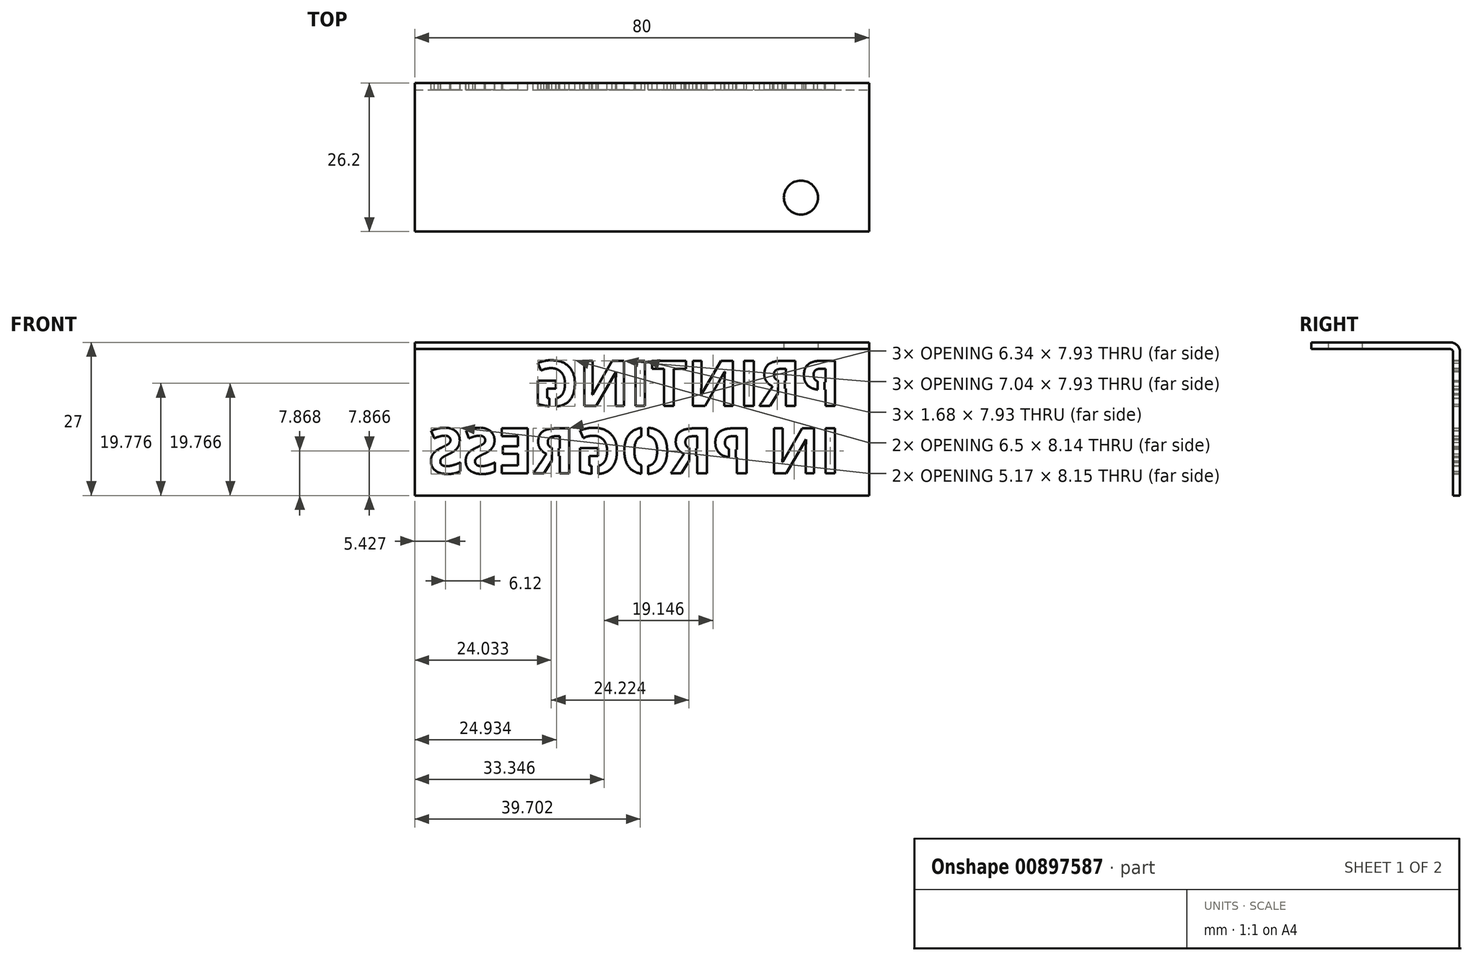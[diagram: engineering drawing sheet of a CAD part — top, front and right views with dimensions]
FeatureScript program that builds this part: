
annotation { "Feature Type Name" : "Feature", "Feature Type Description" : "" }
export const myFeature = defineFeature(function(context is Context, id is Id, definition is map)
    precondition{}
    {
        {
            var Q0;
            Q0=qCreatedBy(makeId("Right.planeOp"),FACE);
            var sketch = newSketch(context, id + "F0", { "sketchPlane" : qUnion([Q0])});
            skLineSegment(sketch, "E0", {"start": v(0, 0) * mm, "end": v(0, 25.8) * mm});
            skLineSegment(sketch, "E1", {"start": v(0, 25.8) * mm, "end": v(-25, 25.8) * mm});
            skLineSegment(sketch, "E2", {"start": v(-25, 25.8) * mm, "end": v(-25, 27) * mm});
            skLineSegment(sketch, "E3", {"start": v(-25, 27) * mm, "end": v(1.2, 27) * mm});
            skLineSegment(sketch, "E4", {"start": v(1.2, 27) * mm, "end": v(1.2, 0) * mm});
            skLineSegment(sketch, "E5", {"start": v(1.2, 0) * mm, "end": v(0, 0) * mm});
            skSolve(sketch);
        }
        {
            var Q0;
            Q0 = qSketchRegion(id + "F0", true);
            extrude(context, id + "F1", {"entities" : qUnion([Q0]), "oppositeDirection" : true, "depth" : 80 * mm, "offsetDistance" : 25 * mm});
        }
        {
            var Q0;
            Q0=makeQuery(id+"F1.opExtrude","SWEPT_EDGE",EDGE,{"disambiguationData":[OSD([sQuery(id+"F0.wireOp",EDGE,"E0"),sQuery(id+"F0.wireOp",EDGE,"E1")])]});
            fillet(context, id + "F2", {"entities" : qUnion([Q0]), "radius" : 0.5 * mm, "tangentPropagation" : true, "allowEdgeOverflow" : false});
        }
        {
            var Q0;
            Q0=makeQuery(id+"F1.opExtrude","SWEPT_EDGE",EDGE,{"disambiguationData":[OSD([sQuery(id+"F0.wireOp",EDGE,"E3"),sQuery(id+"F0.wireOp",EDGE,"E4")])]});
            fillet(context, id + "F3", {"entities" : qUnion([Q0]), "radius" : 1.7 * mm, "tangentPropagation" : true, "allowEdgeOverflow" : false});
        }
        {
            var Q0;
            Q0=makeQuery(id+"F1.opExtrude","SWEPT_FACE",FACE,{"disambiguationData":[OSD([sQuery(id+"F0.wireOp",EDGE,"E1")])]});
            var sketch = newSketch(context, id + "F4", { "sketchPlane" : qUnion([Q0])});
            skCircle(sketch, "E6", {"center": v(-12, 19) * mm, "radius": 3 * mm});
            skSolve(sketch);
        }
        {
            var Q0;
            Q0 = qSketchRegion(id + "F4", true);
            extrude(context, id + "F5", {"entities" : qUnion([Q0]), "operationType" : NewBodyOperationType.REMOVE, "endBound" : BoundingType.THROUGH_ALL, "oppositeDirection" : true, "depth" : 25 * mm, "offsetDistance" : 25 * mm});
        }
        {
            var Q0;
            Q0=makeQuery(id+"F1.opExtrude","SWEPT_FACE",FACE,{"disambiguationData":[OSD([sQuery(id+"F0.wireOp",EDGE,"E4")])]});
            var sketch = newSketch(context, id + "F6", { "sketchPlane" : qUnion([Q0])});
            skText(sketch, "E7", { "text": "PRINTING\n", "fontName": "OpenSans-Bold.ttf"});
            skText(sketch, "E8", { "text": "IN PROGRESS", "fontName": "OpenSans-Bold.ttf"});
            const initialGuessF6  = {"E7": [0.005, 0.0158, 1, 0, 0.008], "E8": [0.005, 0.0039, 1, 0, 0.008]};
            skSetInitialGuess(sketch, initialGuessF6);
            skSolve(sketch);
        }
        {
            var Q0;
            Q0 = qSketchRegion(id + "F6", true);
            extrude(context, id + "F7", {"entities" : qUnion([Q0]), "operationType" : NewBodyOperationType.REMOVE, "oppositeDirection" : true, "depth" : 25 * mm, "offsetDistance" : 25 * mm});
        }
        {
            var Q0;
            {var subQ0=sQuery(id+"F0.wireOp",EDGE,"E5");var subQ1=sQuery(id+"F0.wireOp",EDGE,"E4");Q0=makeQuery(id+"F7.boolean.opBoolean","SPLIT",FACE,{"disambiguationData":[TD([makeQuery(id+"F1.opExtrude","SWEPT_FACE",FACE,{"disambiguationData":[OSD([subQ0])]})])],"derivedFrom":makeQuery(id+"F1.opExtrude","SWEPT_FACE",FACE,{"disambiguationData":[OSD([subQ1])]})});}
            var sketch = newSketch(context, id + "F8", { "sketchPlane" : qUnion([Q0])});
            skLineSegment(sketch, "E9.bottom", {"start": v(7.88, 21.02) * mm, "end": v(9.08, 21.02) * mm});
            skLineSegment(sketch, "E9.top", {"start": v(7.88, 16.73) * mm, "end": v(9.08, 16.73) * mm});
            skLineSegment(sketch, "E9.left", {"start": v(7.88, 21.02) * mm, "end": v(7.88, 16.73) * mm});
            skLineSegment(sketch, "E9.right", {"start": v(9.08, 21.02) * mm, "end": v(9.08, 16.73) * mm});
            skLineSegment(sketch, "E10.bottom", {"start": v(14.86, 21.26) * mm, "end": v(16.06, 21.26) * mm});
            skLineSegment(sketch, "E10.top", {"start": v(14.86, 17.16) * mm, "end": v(16.06, 17.16) * mm});
            skLineSegment(sketch, "E10.left", {"start": v(14.86, 21.26) * mm, "end": v(14.86, 17.16) * mm});
            skLineSegment(sketch, "E10.right", {"start": v(16.06, 21.26) * mm, "end": v(16.06, 17.16) * mm});
            skLineSegment(sketch, "E11.bottom", {"start": v(55.08, 17.67) * mm, "end": v(56.28, 17.67) * mm});
            skLineSegment(sketch, "E11.top", {"start": v(55.08, 14.77) * mm, "end": v(56.28, 14.77) * mm});
            skLineSegment(sketch, "E11.left", {"start": v(55.08, 17.67) * mm, "end": v(55.08, 14.77) * mm});
            skLineSegment(sketch, "E11.right", {"start": v(56.28, 17.67) * mm, "end": v(56.28, 14.77) * mm});
            skLineSegment(sketch, "E12.bottom", {"start": v(23.48, 8.77) * mm, "end": v(24.68, 8.77) * mm});
            skLineSegment(sketch, "E12.top", {"start": v(23.48, 5.41) * mm, "end": v(24.68, 5.41) * mm});
            skLineSegment(sketch, "E12.left", {"start": v(23.48, 8.77) * mm, "end": v(23.48, 5.41) * mm});
            skLineSegment(sketch, "E12.right", {"start": v(24.68, 8.77) * mm, "end": v(24.68, 5.41) * mm});
            skLineSegment(sketch, "E13.bottom", {"start": v(30.46, 9.21) * mm, "end": v(31.66, 9.21) * mm});
            skLineSegment(sketch, "E13.top", {"start": v(30.46, 3.94) * mm, "end": v(31.66, 3.94) * mm});
            skLineSegment(sketch, "E13.left", {"start": v(30.46, 9.21) * mm, "end": v(30.46, 3.94) * mm});
            skLineSegment(sketch, "E13.right", {"start": v(31.66, 9.21) * mm, "end": v(31.66, 3.94) * mm});
            skLineSegment(sketch, "E14.bottom", {"start": v(38.9, 12.7) * mm, "end": v(40.1, 12.7) * mm});
            skLineSegment(sketch, "E14.top", {"start": v(38.9, 3.07) * mm, "end": v(40.1, 3.07) * mm});
            skLineSegment(sketch, "E14.left", {"start": v(38.9, 12.7) * mm, "end": v(38.9, 3.07) * mm});
            skLineSegment(sketch, "E14.right", {"start": v(40.1, 12.7) * mm, "end": v(40.1, 3.07) * mm});
            skLineSegment(sketch, "E15.bottom", {"start": v(54.68, 9.03) * mm, "end": v(55.88, 9.03) * mm});
            skLineSegment(sketch, "E15.top", {"start": v(54.68, 4.68) * mm, "end": v(55.88, 4.68) * mm});
            skLineSegment(sketch, "E15.left", {"start": v(54.68, 9.03) * mm, "end": v(54.68, 4.68) * mm});
            skLineSegment(sketch, "E15.right", {"start": v(55.88, 9.03) * mm, "end": v(55.88, 4.68) * mm});
            skPoint(sketch, "E16", {"position": v(31.66, 5.6) * mm});
            skLineSegment(sketch, "E17.bottom", {"start": v(48.87, 6.12) * mm, "end": v(47.67, 6.12) * mm});
            skLineSegment(sketch, "E17.top", {"start": v(48.87, 3.54) * mm, "end": v(47.67, 3.54) * mm});
            skLineSegment(sketch, "E17.left", {"start": v(48.87, 6.12) * mm, "end": v(48.87, 3.54) * mm});
            skLineSegment(sketch, "E17.right", {"start": v(47.67, 6.12) * mm, "end": v(47.67, 3.54) * mm});
            skPoint(sketch, "E18", {"position": v(49.27, 6.12) * mm});
            skSolve(sketch);
        }
        {
            var Q0;
            Q0 = qSketchRegion(id + "F8", true);
            var Q1;
            {var subQ0=sQuery(id+"F0.wireOp",EDGE,"E5");var subQ5=sQuery(id+"F0.wireOp",EDGE,"E0");Q1=makeQuery(id+"F7.boolean.opBoolean","SPLIT",FACE,{"disambiguationData":[TD([makeQuery(id+"F1.opExtrude","SWEPT_FACE",FACE,{"disambiguationData":[OSD([subQ0])]})])],"derivedFrom":makeQuery(id+"F1.opExtrude","SWEPT_FACE",FACE,{"disambiguationData":[OSD([subQ5])]})});}
            extrude(context, id + "F9", {"entities" : qUnion([Q0]), "operationType" : NewBodyOperationType.ADD, "endBound" : BoundingType.UP_TO_SURFACE, "oppositeDirection" : true, "depth" : 1.2 * mm, "endBoundEntityFace" : qUnion([Q1]), "offsetDistance" : 25 * mm});
        }
    });
